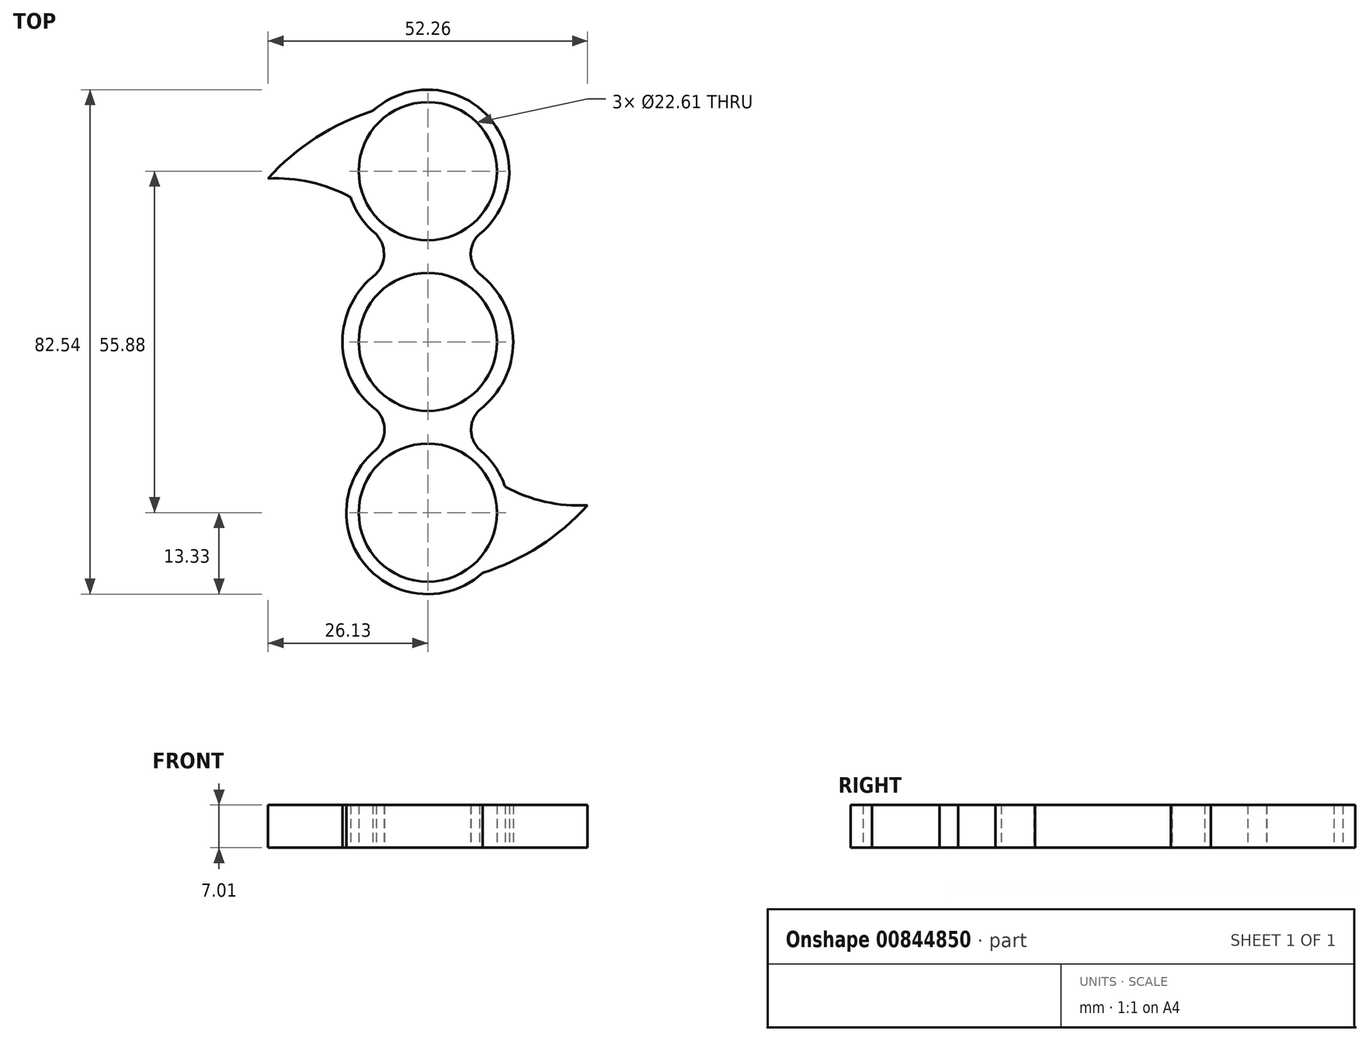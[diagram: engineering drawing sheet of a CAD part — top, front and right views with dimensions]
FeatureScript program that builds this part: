
annotation { "Feature Type Name" : "Feature", "Feature Type Description" : "" }
export const myFeature = defineFeature(function(context is Context, id is Id, definition is map)
    precondition{}
    {
        {
            var Q0;
            Q0=qCreatedBy(makeId("Top.planeOp"),FACE);
            var sketch = newSketch(context, id + "F0", { "sketchPlane" : qUnion([Q0])});
            skCircle(sketch, "E0", {"center": v(0, 0) * mm, "radius": 13.97 * mm});
            skCircle(sketch, "E1", {"center": v(0, 0) * mm, "radius": 11.3 * mm});
            skLineSegment(sketch, "E2", {"start": v(0, 0) * mm, "end": v(0, 27.94) * mm});
            skLineSegment(sketch, "E3", {"start": v(0, 27.94) * mm, "end": v(0, 0) * mm});
            skLineSegment(sketch, "E4", {"start": v(0, 0) * mm, "end": v(0, -27.94) * mm});
            skCircle(sketch, "E5", {"center": v(0, 27.94) * mm, "radius": 13.34 * mm});
            skCircle(sketch, "E6", {"center": v(0, -27.94) * mm, "radius": 13.34 * mm});
            skArc(sketch, "E7", {"start": v(-8.44, 11.13) * mm, "mid": v(-7.17, 14.38) * mm, "end": v(-8.46, 17.63) * mm});
            skArc(sketch, "E8", {"start": v(8.46, 17.63) * mm, "mid": v(7.02, 14.38) * mm, "end": v(8.44, 11.13) * mm});
            skArc(sketch, "E9", {"start": v(-8.44, -17.62) * mm, "mid": v(-7.1, -14.37) * mm, "end": v(-8.44, -11.13) * mm});
            skArc(sketch, "E10", {"start": v(8.44, -11.13) * mm, "mid": v(7.08, -14.37) * mm, "end": v(8.44, -17.62) * mm});
            skCircle(sketch, "E11", {"center": v(0, -27.94) * mm, "radius": 11.3 * mm});
            skCircle(sketch, "E12", {"center": v(0, 27.94) * mm, "radius": 11.3 * mm});
            skPoint(sketch, "E13", {"position": v(-8.97, 37.8) * mm});
            skPoint(sketch, "E14", {"position": v(-26.13, 26.73) * mm});
            skPoint(sketch, "E15", {"position": v(-12.64, 23.7) * mm});
            skArc(sketch, "E16", {"start": v(-8.97, 37.8) * mm, "mid": v(-18.3, 33.42) * mm, "end": v(-26.13, 26.73) * mm});
            skArc(sketch, "E17", {"start": v(-12.64, 23.7) * mm, "mid": v(-19.17, 26.15) * mm, "end": v(-26.13, 26.73) * mm});
            skArc(sketch, "E18.2.0", {"start": v(8.97, -37.8) * mm, "mid": v(18.3, -33.42) * mm, "end": v(26.13, -26.73) * mm});
            skArc(sketch, "E18.2.1", {"start": v(12.64, -23.7) * mm, "mid": v(19.17, -26.15) * mm, "end": v(26.13, -26.73) * mm});
            skSolve(sketch);
        }
        {
            var Q0;
            Q0=makeQuery(id+"F0.imprint","IMPRINT",FACE,{"disambiguationData":[TD([[makeQuery(id+"F0.imprint","IMPRINT",EDGE,{"derivedFrom":sQuery(id+"F0.wireOp",EDGE,"E12")}),-1.0]])]});
            var Q1;
            {var subQ0=sQuery(id+"F0.wireOp",EDGE,"E16");Q1=makeQuery(id+"F0.imprint","IMPRINT",FACE,{"disambiguationData":[TD([[makeQuery(id+"F0.imprint","IMPRINT",EDGE,{"derivedFrom":subQ0}),1.0]])]});}
            var Q2;
            {var subQ0=sQuery(id+"F0.wireOp",EDGE,"E7");Q2=makeQuery(id+"F0.imprint","IMPRINT",FACE,{"disambiguationData":[TD([[makeQuery(id+"F0.imprint","IMPRINT",EDGE,{"derivedFrom":subQ0}),-1.0]])]});}
            var Q3;
            {var subQ0=sQuery(id+"F0.wireOp",EDGE,"E0");var subQ4=makeQuery(id+"F0.imprint","INTERSECT",VERTEX,{"derivedFrom":[subQ0,sQuery(id+"F0.wireOp",EDGE,"E7")]});Q3=makeQuery(id+"F0.imprint","IMPRINT",FACE,{"disambiguationData":[TD([[makeQuery(id+"F0.imprint","IMPRINT",EDGE,{"disambiguationData":[TD([[subQ4,1.0]])],"derivedFrom":subQ0}),1.0]])]});}
            var Q4;
            {var subQ5=sQuery(id+"F0.wireOp",EDGE,"E0");var subQ8=makeQuery(id+"F0.imprint","INTERSECT",VERTEX,{"derivedFrom":[subQ5,sQuery(id+"F0.wireOp",EDGE,"E8")]});Q4=makeQuery(id+"F0.imprint","IMPRINT",FACE,{"disambiguationData":[TD([[makeQuery(id+"F0.imprint","IMPRINT",EDGE,{"disambiguationData":[TD([[subQ8,-1.0]])],"derivedFrom":subQ5}),1.0]])]});}
            var Q5;
            {var subQ0=sQuery(id+"F0.wireOp",EDGE,"E8");Q5=makeQuery(id+"F0.imprint","IMPRINT",FACE,{"disambiguationData":[TD([[makeQuery(id+"F0.imprint","IMPRINT",EDGE,{"derivedFrom":subQ0}),-1.0]])]});}
            var Q6;
            {var subQ0=sQuery(id+"F0.wireOp",EDGE,"E10");Q6=makeQuery(id+"F0.imprint","IMPRINT",FACE,{"disambiguationData":[TD([[makeQuery(id+"F0.imprint","IMPRINT",EDGE,{"derivedFrom":subQ0}),-1.0]])]});}
            var Q7;
            {var subQ0=sQuery(id+"F0.wireOp",EDGE,"E9");Q7=makeQuery(id+"F0.imprint","IMPRINT",FACE,{"disambiguationData":[TD([[makeQuery(id+"F0.imprint","IMPRINT",EDGE,{"derivedFrom":subQ0}),-1.0]])]});}
            var Q8;
            Q8=makeQuery(id+"F0.imprint","IMPRINT",FACE,{"disambiguationData":[TD([[makeQuery(id+"F0.imprint","IMPRINT",EDGE,{"derivedFrom":sQuery(id+"F0.wireOp",EDGE,"E11")}),-1.0]])]});
            var Q9;
            {var subQ0=sQuery(id+"F0.wireOp",EDGE,"E18.2.0");Q9=makeQuery(id+"F0.imprint","IMPRINT",FACE,{"disambiguationData":[TD([[makeQuery(id+"F0.imprint","IMPRINT",EDGE,{"derivedFrom":subQ0}),1.0]])]});}
            extrude(context, id + "F1", {"entities" : qUnion([Q0, Q1, Q2, Q3, Q4, Q5, Q6, Q7, Q8, Q9]), "depth" : 7 * mm, "offsetDistance" : 25.4 * mm});
        }
    });
